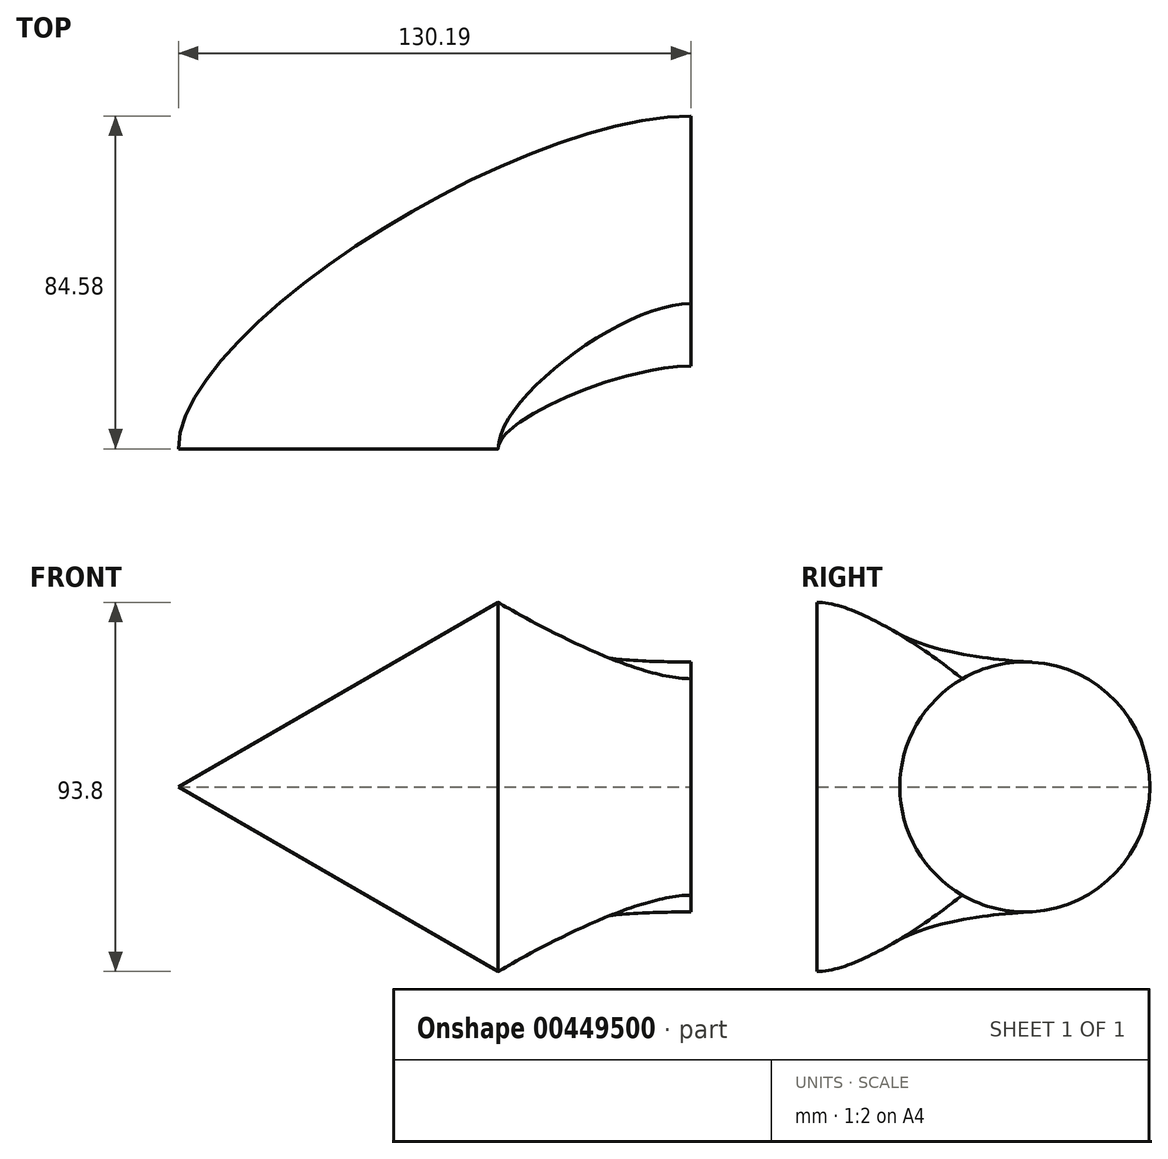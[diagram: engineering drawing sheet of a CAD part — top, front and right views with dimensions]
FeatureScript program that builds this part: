
annotation { "Feature Type Name" : "Feature", "Feature Type Description" : "" }
export const myFeature = defineFeature(function(context is Context, id is Id, definition is map)
    precondition{}
    {
        {
            var Q0;
            Q0=qCreatedBy(makeId("Front.planeOp"),FACE);
            var sketch = newSketch(context, id + "F0", { "sketchPlane" : qUnion([Q0])});
            skLineSegment(sketch, "E0", {"start": v(0, 0) * mm, "end": v(-76.03, 0) * mm, "construction": true});
            skCircle(sketch, "E1.cCircle", {"center": v(-76.03, 0) * mm, "radius": 27.08 * mm, "construction": true});
            skLineSegment(sketch, "E1.0", {"start": v(-48.95, 46.9) * mm, "end": v(-48.95, -46.9) * mm});
            skLineSegment(sketch, "E1.1", {"start": v(-48.95, -46.9) * mm, "end": v(-130.19, 0) * mm});
            skLineSegment(sketch, "E1.2", {"start": v(-130.19, 0) * mm, "end": v(-48.95, 46.9) * mm});
            skPoint(sketch, "E1.0.midPoint", {"position": v(-48.95, 0) * mm});
            skSolve(sketch);
        }
        {
            var Q0;
            Q0=qCreatedBy(makeId("Right.planeOp"),FACE);
            var sketch = newSketch(context, id + "F1", { "sketchPlane" : qUnion([Q0])});
            skLineSegment(sketch, "E2", {"start": v(0, 0) * mm, "end": v(52.83, 0) * mm, "construction": true});
            skCircle(sketch, "E3.cCircle", {"center": v(52.83, 0) * mm, "radius": 15.87 * mm, "construction": true});
            skLineSegment(sketch, "E3.0", {"start": v(36.96, -27.5) * mm, "end": v(36.96, 27.5) * mm, "construction": true});
            skLineSegment(sketch, "E3.1", {"start": v(36.96, 27.5) * mm, "end": v(84.58, 0) * mm, "construction": true});
            skLineSegment(sketch, "E3.2", {"start": v(84.58, 0) * mm, "end": v(36.96, -27.5) * mm, "construction": true});
            skPoint(sketch, "E3.0.midPoint", {"position": v(36.96, 0) * mm});
            skArc(sketch, "E4", {"start": v(36.96, -27.5) * mm, "mid": v(68.7, -27.5) * mm, "end": v(84.58, 0) * mm});
            skArc(sketch, "E5", {"start": v(36.96, 27.5) * mm, "mid": v(21.08, 0) * mm, "end": v(36.96, -27.5) * mm});
            skArc(sketch, "E6", {"start": v(84.58, 0) * mm, "mid": v(68.7, 27.5) * mm, "end": v(36.96, 27.5) * mm});
            skSolve(sketch);
        }
        {
            var Q0;
            Q0 = qSketchRegion(id + "F0", true);
            var Q1;
            Q1 = qSketchRegion(id + "F1", true);
            loft(context, id + "F2", {"startCondition" : LoftEndDerivativeType.NORMAL_TO_PROFILE, "startMagnitude" : 1, "endCondition" : LoftEndDerivativeType.NORMAL_TO_PROFILE, "endMagnitude" : 1, "sheetProfilesArray" : [{ "sheetProfileEntities" : qUnion([Q0]) }, { "sheetProfileEntities" : qUnion([Q1]) }]});
        }
    });
